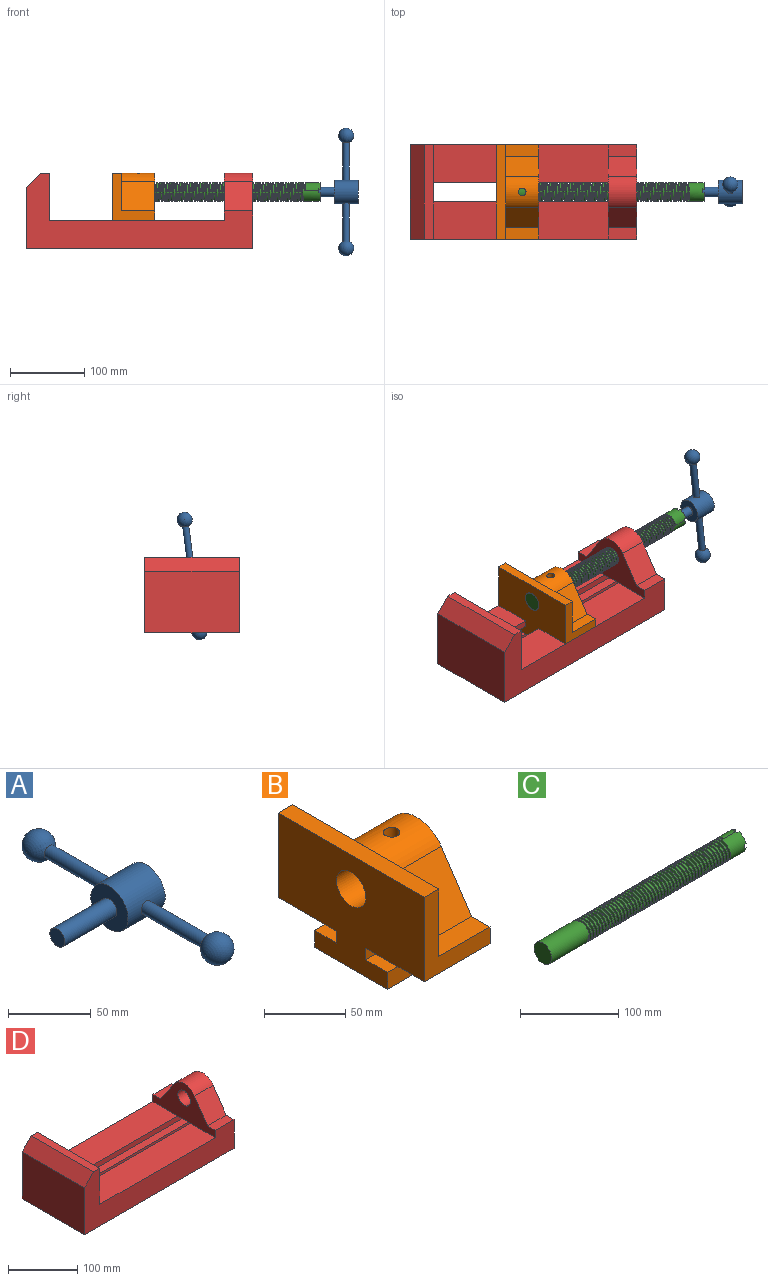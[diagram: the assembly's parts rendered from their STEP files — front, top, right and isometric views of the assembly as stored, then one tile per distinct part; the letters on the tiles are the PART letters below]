
ASSEMBLY  parts=4 mates=3
PART A: 9 faces, bbox 76.2x172.7x31.8 mm
  f0: cylinder r=4.45mm len=51.82mm, axis (0,1,0), area 1438.5mm2, adj f2,f8
  f1: cylinder r=4.45mm len=51.82mm, axis (0,1,0), area 1438.5mm2, adj f2,f7
  f2: cylinder r=15.88mm len=31.75mm, axis (1,0,0), area 3041.4mm2, adj f0,f1,f3,f4
  f3: plane 31.75x31.75mm, normal (-1,0,0), area 665.1mm2, adj f2,f5
  f4: plane 31.75x31.75mm, normal (1,0,0), area 791.7mm2, adj f2
  f5: cylinder r=6.35mm len=44.45mm, axis (1,0,0), area 1773.5mm2, adj f3,f6
  f6: plane 12.7x12.7mm, normal (-1,0,0), area 126.7mm2, adj f5
  f7: sphere r=10.16mm, area 1231.8mm2, adj f1
  f8: sphere r=10.16mm, area 1231.8mm2, adj f0
PART B: 23 faces, bbox 57.2x127x85.1 mm
  f0: cylinder r=12.7mm len=57.15mm, axis (-1,0,0), area 4477.8mm2, adj f17,f18,f22
  f1: plane 44.45x15.88mm, normal (0,0,1), area 705.6mm2, adj f2,f16,f17,f20
  f2: plane 44.45x39.55mm, normal (0,0.83,0.56), area 2116.9mm2, adj f1,f3,f17,f20
  f3: cylinder r=25.4mm len=44.45mm, axis (-1,0,0), area 2131.3mm2, adj f2,f4,f17,f20,f21,f22
  f4: plane 44.45x39.55mm, normal (0,-0.83,0.56), area 2116.9mm2, adj f3,f5,f17,f21
  f5: plane 44.45x15.88mm, normal (0,0,1), area 705.6mm2, adj f4,f6,f17,f21
  f6: plane 63.5x57.15mm, normal (0,-1,0), area 1371mm2, adj f5,f7,f17,f18,f19,f21
  f7: plane 57.15x50.8mm, normal (0,0,-1), area 2903.2mm2, adj f6,f8,f17,f18
  f8: plane 57.15x8.89mm, normal (0,-1,0), area 508.1mm2, adj f7,f9,f17,f18
  f9: plane 57.15x19.05mm, normal (0,0,1), area 1088.7mm2, adj f8,f10,f17,f18
  f10: plane 57.15x12.7mm, normal (0,-1,0), area 725.8mm2, adj f9,f11,f17,f18
  f11: plane 63.5x57.15mm, normal (0,0,-1), area 3629mm2, adj f10,f12,f17,f18
  f12: plane 57.15x12.7mm, normal (0,1,0), area 725.8mm2, adj f11,f13,f17,f18
  f13: plane 57.15x19.05mm, normal (0,0,1), area 1088.7mm2, adj f12,f14,f17,f18
  f14: plane 57.15x8.89mm, normal (0,1,0), area 508.1mm2, adj f13,f15,f17,f18
  f15: plane 57.15x50.8mm, normal (0,0,-1), area 2903.2mm2, adj f14,f16,f17,f18
  f16: plane 63.5x57.15mm, normal (0,1,0), area 1371mm2, adj f1,f15,f17,f18,f19,f20
  f17: plane 127x85.09mm, normal (1,0,0), area 5190mm2, adj f0,f1,f2,f3,f4,f5,f6,f7
  f18: plane 127x85.09mm, normal (-1,0,0), area 8590mm2, adj f0,f6,f7,f8,f9,f10,f11,f12
  f19: plane 127x12.7mm, normal (0,0,1), area 1612.9mm2, adj f6,f16,f18,f20,f21
  f20: plane 63.5x50.8mm, normal (1,0,0), area 1700mm2, adj f1,f2,f3,f16,f19
  f21: plane 63.5x50.8mm, normal (1,0,0), area 1700mm2, adj f3,f4,f5,f6,f19
  f22: cylinder r=5.08mm len=13.76mm, axis (0,0,1), area 413.9mm2, adj f0,f3
PART C: 72 faces, bbox 279.6x27.3x29.3 mm
  f0: plane 9.9x9.9mm, normal (1,0,0), area 62.3mm2, adj f4,f59,f61,f70
  f1: plane 9.9x9.9mm, normal (1,0,0), area 62.3mm2, adj f4,f58,f67,f70
  f2: plane 9.9x9.9mm, normal (1,0,0), area 62.3mm2, adj f4,f65,f68,f70
  f3: cylinder r=12.7mm len=57.79mm, axis (-1,0,0), area 4335.1mm2, adj f49,f53,f54,f56,f57
  f4: cylinder r=12.7mm len=25.4mm, axis (-1,0,0), area 1644.3mm2, adj f0,f1,f2,f5,f50,f51,f53,f54
  f5: cylinder r=12.7mm len=25.4mm, axis (-1,0,0), area 151.7mm2, adj f4,f6,f53,f54
  f6: cylinder r=12.7mm len=25.4mm, axis (-1,0,0), area 151.7mm2, adj f5,f7,f53,f54
  f7: cylinder r=12.7mm len=25.4mm, axis (-1,0,0), area 151.6mm2, adj f6,f8,f53,f54
  f8: cylinder r=12.7mm len=25.4mm, axis (-1,0,0), area 151.7mm2, adj f7,f9,f53,f54
  f9: cylinder r=12.7mm len=25.4mm, axis (-1,0,0), area 151.7mm2, adj f8,f10,f53,f54
  f10: cylinder r=12.7mm len=25.4mm, axis (-1,0,0), area 151.6mm2, adj f9,f11,f53,f54
  f11: cylinder r=12.7mm len=25.4mm, axis (-1,0,0), area 151.7mm2, adj f10,f12,f53,f54
  f12: cylinder r=12.7mm len=25.4mm, axis (-1,0,0), area 151.7mm2, adj f11,f13,f53,f54
  f13: cylinder r=12.7mm len=25.4mm, axis (-1,0,0), area 151.6mm2, adj f12,f14,f53,f54
  f14: cylinder r=12.7mm len=25.4mm, axis (-1,0,0), area 151.7mm2, adj f13,f15,f53,f54
  f15: cylinder r=12.7mm len=25.4mm, axis (-1,0,0), area 151.7mm2, adj f14,f16,f53,f54
  f16: cylinder r=12.7mm len=25.4mm, axis (-1,0,0), area 151.6mm2, adj f15,f17,f53,f54
  f17: cylinder r=12.7mm len=25.4mm, axis (-1,0,0), area 151.7mm2, adj f16,f18,f53,f54
  f18: cylinder r=12.7mm len=25.4mm, axis (-1,0,0), area 151.7mm2, adj f17,f19,f53,f54
  f19: cylinder r=12.7mm len=25.4mm, axis (-1,0,0), area 151.6mm2, adj f18,f20,f53,f54
  f20: cylinder r=12.7mm len=25.4mm, axis (-1,0,0), area 151.7mm2, adj f19,f21,f53,f54
  f21: cylinder r=12.7mm len=25.4mm, axis (-1,0,0), area 151.6mm2, adj f20,f22,f53,f54
  f22: cylinder r=12.7mm len=25.4mm, axis (-1,0,0), area 151.6mm2, adj f21,f23,f53,f54
  f23: cylinder r=12.7mm len=25.4mm, axis (-1,0,0), area 151.7mm2, adj f22,f24,f53,f54
  f24: cylinder r=12.7mm len=25.4mm, axis (-1,0,0), area 151.6mm2, adj f23,f25,f53,f54
  f25: cylinder r=12.7mm len=25.4mm, axis (-1,0,0), area 151.6mm2, adj f24,f26,f53,f54
  f26: cylinder r=12.7mm len=25.4mm, axis (-1,0,0), area 151.7mm2, adj f25,f27,f53,f54
  f27: cylinder r=12.7mm len=25.4mm, axis (-1,0,0), area 151.6mm2, adj f26,f28,f53,f54
  f28: cylinder r=12.7mm len=25.4mm, axis (-1,0,0), area 151.6mm2, adj f27,f29,f53,f54
  f29: cylinder r=12.7mm len=25.4mm, axis (-1,0,0), area 151.7mm2, adj f28,f30,f53,f54
  f30: cylinder r=12.7mm len=25.4mm, axis (-1,0,0), area 151.6mm2, adj f29,f31,f53,f54
  f31: cylinder r=12.7mm len=25.4mm, axis (-1,0,0), area 151.7mm2, adj f30,f32,f53,f54
  f32: cylinder r=12.7mm len=25.4mm, axis (-1,0,0), area 151.7mm2, adj f31,f33,f53,f54
  f33: cylinder r=12.7mm len=25.4mm, axis (-1,0,0), area 151.6mm2, adj f32,f34,f53,f54
  f34: cylinder r=12.7mm len=25.4mm, axis (-1,0,0), area 151.7mm2, adj f33,f35,f53,f54
  f35: cylinder r=12.7mm len=25.4mm, axis (-1,0,0), area 151.7mm2, adj f34,f36,f53,f54
  f36: cylinder r=12.7mm len=25.4mm, axis (-1,0,0), area 151.6mm2, adj f35,f37,f53,f54
  f37: cylinder r=12.7mm len=25.4mm, axis (-1,0,0), area 151.7mm2, adj f36,f38,f53,f54
  f38: cylinder r=12.7mm len=25.4mm, axis (-1,0,0), area 151.7mm2, adj f37,f39,f53,f54
  f39: cylinder r=12.7mm len=25.4mm, axis (-1,0,0), area 151.6mm2, adj f38,f40,f53,f54
  f40: cylinder r=12.7mm len=25.4mm, axis (-1,0,0), area 151.7mm2, adj f39,f41,f53,f54
  f41: cylinder r=12.7mm len=25.4mm, axis (-1,0,0), area 151.7mm2, adj f40,f42,f53,f54
  f42: cylinder r=12.7mm len=25.4mm, axis (-1,0,0), area 151.6mm2, adj f41,f43,f53,f54
  f43: cylinder r=12.7mm len=25.4mm, axis (-1,0,0), area 151.7mm2, adj f42,f44,f53,f54
  f44: cylinder r=12.7mm len=25.4mm, axis (-1,0,0), area 151.7mm2, adj f43,f45,f53,f54
  f45: cylinder r=12.7mm len=25.4mm, axis (-1,0,0), area 151.6mm2, adj f44,f46,f53,f54
  f46: cylinder r=12.7mm len=25.4mm, axis (-1,0,0), area 151.7mm2, adj f45,f47,f53,f54
  f47: cylinder r=12.7mm len=25.4mm, axis (-1,0,0), area 151.7mm2, adj f46,f48,f53,f54
  f48: cylinder r=12.7mm len=25.4mm, axis (-1,0,0), area 151.6mm2, adj f47,f49,f53,f54
  f49: cylinder r=12.7mm len=25.4mm, axis (-1,0,0), area 151.7mm2, adj f3,f48,f53,f54
  f50: plane 16.54x0.1mm, normal (0,-0.22,0.98), area 1.2mm2, adj f4,f53
  f51: plane 9.9x9.9mm, normal (1,0,0), area 62.3mm2, adj f4,f62,f64,f70
  f52: bspline ~209.44x23.28mm, area 3770.2mm2, adj f53,f54,f55,f57
  f53: bspline ~208.81x29.06mm, area 8799mm2, adj f3,f4,f5,f6,f7,f8,f9,f10
  f54: bspline ~206.64x25.39mm, area 8758mm2, adj f3,f4,f5,f6,f7,f8,f9,f10
  f55: plane 2.56x2.55mm, normal (-0.06,1,0), area 4.8mm2, adj f4,f52,f53,f54
  f56: plane 25.4x25.4mm, normal (-1,0,0), area 506.7mm2, adj f3
  f57: plane 25.59x16.93mm, normal (1,0,0), area 79.2mm2, adj f3,f52,f53,f54
  f58: plane 6.62x2.54mm, normal (0,1,0), area 16.8mm2, adj f1,f4,f60,f70
  f59: plane 6.62x2.54mm, normal (0,-1,0), area 16.8mm2, adj f0,f4,f60,f70
  f60: plane 6.88x5.08mm, normal (1,0,0), area 32.7mm2, adj f4,f58,f59,f70
  f61: plane 6.62x2.54mm, normal (0,0,-1), area 16.8mm2, adj f0,f4,f63,f70
  f62: plane 6.62x2.54mm, normal (0,0,1), area 16.8mm2, adj f4,f51,f63,f70
  f63: plane 6.88x5.08mm, normal (1,0,0), area 32.7mm2, adj f4,f61,f62,f70
  f64: plane 6.62x2.54mm, normal (0,-1,0), area 16.8mm2, adj f4,f51,f66,f70
  f65: plane 6.62x2.54mm, normal (0,1,0), area 16.8mm2, adj f2,f4,f66,f70
  f66: plane 6.88x5.08mm, normal (1,0,0), area 32.7mm2, adj f4,f64,f65,f70
  f67: plane 6.62x2.54mm, normal (0,0,-1), area 16.8mm2, adj f1,f4,f69,f70
  f68: plane 6.62x2.54mm, normal (0,0,1), area 16.8mm2, adj f2,f4,f69,f70
  f69: plane 6.88x5.08mm, normal (1,0,0), area 32.7mm2, adj f4,f67,f68,f70
  f70: cylinder r=6.35mm len=25.4mm, axis (1,0,0), area 960.3mm2, adj f0,f1,f2,f51,f58,f59,f60,f61
  f71: plane 12.7x12.7mm, normal (1,0,0), area 126.7mm2, adj f70
PART D: 28 faces, bbox 304.8x127x101.6 mm
  f0: plane 273.05x12.7mm, normal (0,1,0), area 3467.7mm2, adj f1,f7,f22,f24
  f1: plane 273.05x19.05mm, normal (0,0,-1), area 5201.6mm2, adj f0,f2,f22,f24
  f2: plane 273.05x8.89mm, normal (0,1,0), area 2427.4mm2, adj f1,f3,f20,f22,f24
  f3: plane 234.95x50.8mm, normal (0,0,1), area 11935.5mm2, adj f2,f4,f23,f24
  f4: plane 304.8x101.6mm, normal (0,-1,0), area 13931.4mm2, adj f3,f5,f19,f22,f23,f24,f25,f26
  f5: plane 304.8x127mm, normal (0,0,-1), area 31774.1mm2, adj f4,f6,f10,f11,f22,f24,f26
  f6: plane 273.05x16.51mm, normal (0,1,0), area 4508.1mm2, adj f5,f7,f22,f24
  f7: plane 273.05x19.05mm, normal (0,0,1), area 5201.6mm2, adj f0,f6,f22,f24
  f8: plane 273.05x12.7mm, normal (0,-1,0), area 3467.7mm2, adj f9,f14,f22,f24
  f9: plane 273.05x19.05mm, normal (0,0,1), area 5201.6mm2, adj f8,f10,f22,f24
  f10: plane 273.05x16.51mm, normal (0,-1,0), area 4508.1mm2, adj f5,f9,f22,f24
  f11: plane 304.8x101.6mm, normal (0,1,0), area 13931.4mm2, adj f5,f12,f15,f22,f23,f24,f25,f26
  f12: plane 234.95x50.8mm, normal (0,0,1), area 11935.5mm2, adj f11,f13,f23,f24
  f13: plane 273.05x8.89mm, normal (0,-1,0), area 2427.4mm2, adj f12,f14,f20,f22,f24
  f14: plane 273.05x19.05mm, normal (0,0,-1), area 5201.6mm2, adj f8,f13,f22,f24
  f15: plane 38.1x15.88mm, normal (0,0,1), area 604.8mm2, adj f11,f16,f22,f23
  f16: plane 39.55x38.1mm, normal (0,0.83,0.56), area 1814.5mm2, adj f15,f17,f22,f23
  f17: cylinder r=25.4mm len=42.19mm, axis (-1,0,0), area 1896.6mm2, adj f16,f18,f22,f23
  f18: plane 39.55x38.1mm, normal (0,-0.83,0.56), area 1814.5mm2, adj f17,f19,f22,f23
  f19: plane 38.1x15.88mm, normal (0,0,1), area 604.8mm2, adj f4,f18,f22,f23
  f20: plane 38.1x25.4mm, normal (0,0,-1), area 967.7mm2, adj f2,f13,f22,f23
  f21: cylinder r=12.7mm len=38.1mm, axis (-1,0,0), area 3040.2mm2, adj f22,f23
  f22: plane 127x101.6mm, normal (1,0,0), area 7544.8mm2, adj f0,f1,f2,f4,f5,f6,f7,f8
  f23: plane 127x63.5mm, normal (-1,0,0), area 4157.7mm2, adj f3,f4,f11,f12,f15,f16,f17,f18
  f24: plane 127x101.6mm, normal (1,0,0), area 9516.1mm2, adj f0,f1,f2,f3,f4,f5,f6,f7
  f25: plane 127x12.7mm, normal (0,0,1), area 1612.9mm2, adj f4,f11,f24,f27
  f26: plane 127x82.55mm, normal (-1,0,0), area 10483.9mm2, adj f4,f5,f11,f27
  f27: plane 127x19.05mm, normal (-0.71,0,0.71), area 3421.5mm2, adj f4,f11,f25,f26
PLACE A rot(axis=(1,0,0),82.6deg) t=(460.61,-64.25,-22.79)mm
PLACE B t=(381.23,-64.25,-79.94)mm
PLACE C rot(axis=(1,0,0),82.6deg) t=(198.73,-64.25,-22.79)mm
PLACE D t=(297.11,-64.25,-79.94)mm fixed
MATE revolute B.f0 <-> C.f3  axis (-1,0,0) through (146.28,-64.25,-22.79)mm
MATE slider B.f0 <-> D.f17  axis (-1,0,0) through (203.43,-64.25,-22.79)mm
MATE fastened A.f2 <-> C.f3  axis (-1,0,0) through (400.28,-64.25,-22.79)mm
